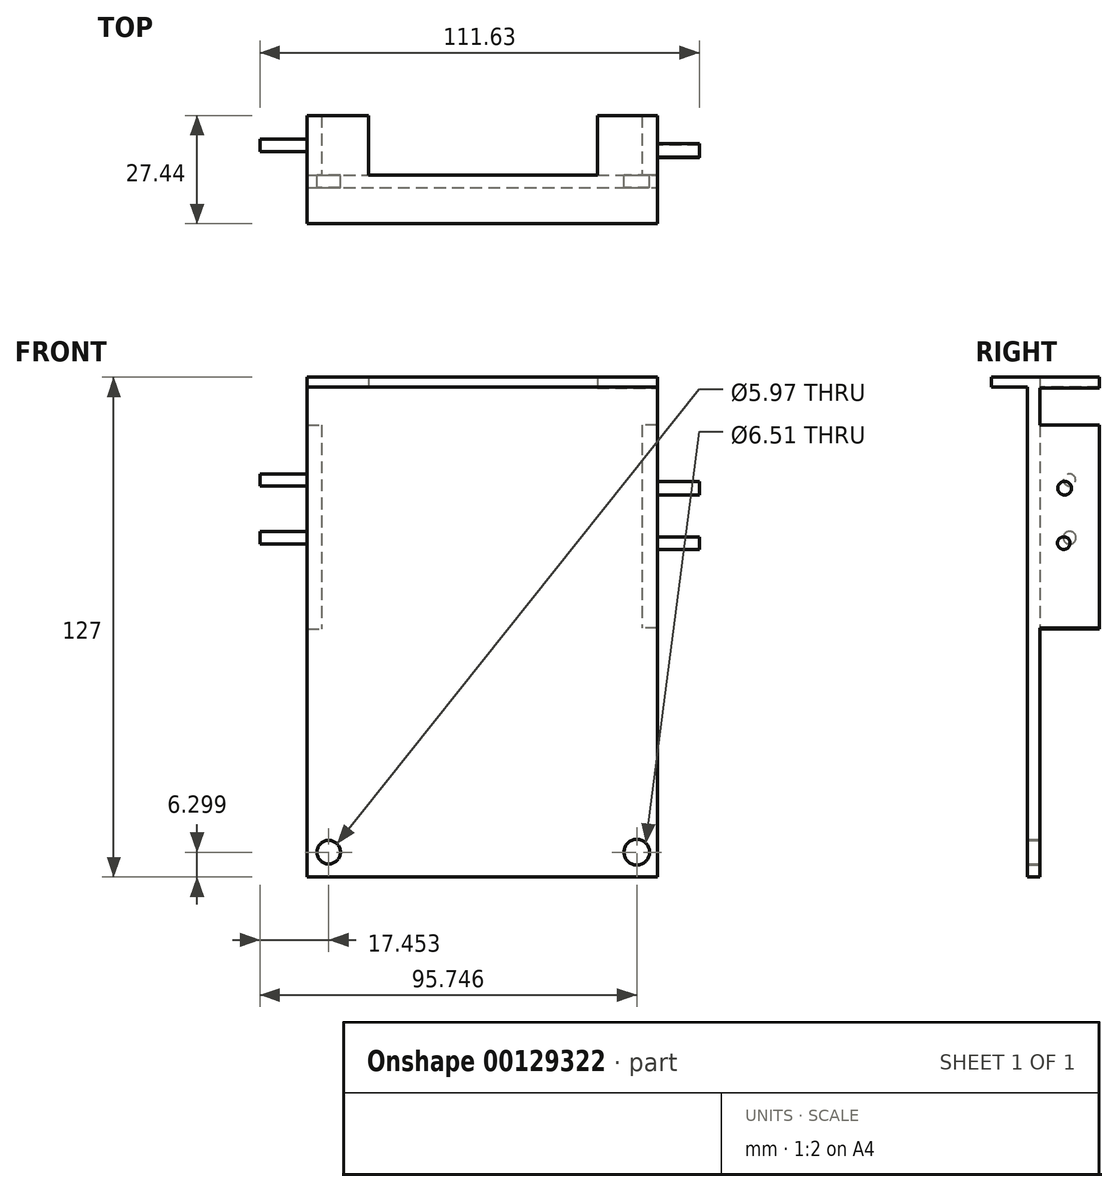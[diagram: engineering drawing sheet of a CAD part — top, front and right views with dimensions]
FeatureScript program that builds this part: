
annotation { "Feature Type Name" : "Feature", "Feature Type Description" : "" }
export const myFeature = defineFeature(function(context is Context, id is Id, definition is map)
    precondition{}
    {
        {
            var Q0;
            Q0=qCreatedBy(makeId("Front.planeOp"),FACE);
            var sketch = newSketch(context, id + "F0", { "sketchPlane" : qUnion([Q0])});
            skLineSegment(sketch, "E0.bottom", {"start": v(-44.56, 55.8) * mm, "end": v(44.34, 55.8) * mm});
            skLineSegment(sketch, "E0.top", {"start": v(-44.56, -71.2) * mm, "end": v(44.34, -71.2) * mm});
            skLineSegment(sketch, "E0.left", {"start": v(-44.56, 55.8) * mm, "end": v(-44.56, -71.2) * mm});
            skLineSegment(sketch, "E0.right", {"start": v(44.34, 55.8) * mm, "end": v(44.34, -71.2) * mm});
            skCircle(sketch, "E1", {"center": v(-39.15, -64.9) * mm, "radius": 2.98 * mm});
            skCircle(sketch, "E2", {"center": v(39.15, -64.9) * mm, "radius": 3.25 * mm});
            skSolve(sketch);
        }
        {
            var Q0;
            Q0=makeQuery(id+"F0.imprint","IMPRINT",FACE,{"disambiguationData":[TD([[makeQuery(id+"F0.imprint","IMPRINT",EDGE,{"derivedFrom":sQuery(id+"F0.wireOp",EDGE,"E0.bottom")}),-1.0]])]});
            extrude(context, id + "F1", {"entities" : qUnion([Q0]), "depth" : 3.17 * mm});
        }
        {
            var Q0;
            Q0=makeQuery(id+"F1.opExtrude","CAP_FACE",FACE,{"disambiguationData":[OSD([sQuery(id+"F0.wireOp",EDGE,"E0.bottom"),sQuery(id+"F0.wireOp",EDGE,"E0.top"),sQuery(id+"F0.wireOp",EDGE,"E0.left"),sQuery(id+"F0.wireOp",EDGE,"E0.right")])],"isStart":false});
            var sketch = newSketch(context, id + "F2", { "sketchPlane" : qUnion([Q0])});
            skLineSegment(sketch, "E3.bottom", {"start": v(-44.56, 55.8) * mm, "end": v(44.34, 55.8) * mm});
            skLineSegment(sketch, "E3.top", {"start": v(-44.56, 53.26) * mm, "end": v(44.34, 53.26) * mm});
            skLineSegment(sketch, "E3.left", {"start": v(-44.56, 55.8) * mm, "end": v(-44.56, 53.26) * mm});
            skLineSegment(sketch, "E3.right", {"start": v(44.34, 55.8) * mm, "end": v(44.34, 53.26) * mm});
            skSolve(sketch);
        }
        {
            var Q0;
            Q0=makeQuery(id+"F2.imprint","IMPRINT",FACE,{"disambiguationData":[TD([[makeQuery(id+"F2.imprint","IMPRINT",EDGE,{"derivedFrom":sQuery(id+"F2.wireOp",EDGE,"E3.bottom")}),-1.0]])]});
            extrude(context, id + "F3", {"entities" : qUnion([Q0]), "operationType" : NewBodyOperationType.ADD, "depth" : 9.15 * mm});
        }
        {
            var Q0;
            Q0=makeQuery(id+"F1.opExtrude","CAP_FACE",FACE,{"disambiguationData":[OSD([sQuery(id+"F0.wireOp",EDGE,"E0.bottom"),sQuery(id+"F0.wireOp",EDGE,"E0.top"),sQuery(id+"F0.wireOp",EDGE,"E0.left"),sQuery(id+"F0.wireOp",EDGE,"E0.right")])],"isStart":true});
            var sketch = newSketch(context, id + "F4", { "sketchPlane" : qUnion([Q0])});
            skLineSegment(sketch, "E4.left", {"start": v(-29.1, 55.8) * mm, "end": v(-29.1, 55.42) * mm});
            skLineSegment(sketch, "E4.right", {"start": v(-44.34, 55.8) * mm, "end": v(-44.34, 55.42) * mm});
            skLineSegment(sketch, "E5.bottom", {"start": v(-41.66, 55.42) * mm, "end": v(-44.34, 55.42) * mm});
            skLineSegment(sketch, "E6.bottom", {"start": v(-29.1, 55.8) * mm, "end": v(-44.34, 55.8) * mm});
            skLineSegment(sketch, "E6.top", {"start": v(-29.1, 53) * mm, "end": v(-44.34, 53) * mm});
            skLineSegment(sketch, "E6.left", {"start": v(-29.1, 55.8) * mm, "end": v(-29.1, 53) * mm});
            skLineSegment(sketch, "E6.right", {"start": v(-44.34, 55.8) * mm, "end": v(-44.34, 53) * mm});
            skLineSegment(sketch, "E7.bottom", {"start": v(44.56, 55.8) * mm, "end": v(29.07, 55.8) * mm});
            skLineSegment(sketch, "E7.top", {"start": v(44.56, 53.23) * mm, "end": v(29.07, 53.23) * mm});
            skLineSegment(sketch, "E7.left", {"start": v(44.56, 55.8) * mm, "end": v(44.56, 53.23) * mm});
            skLineSegment(sketch, "E7.right", {"start": v(29.07, 55.8) * mm, "end": v(29.07, 53.23) * mm});
            skLineSegment(sketch, "E8.bottom", {"start": v(40.75, 53.23) * mm, "end": v(44.56, 53.23) * mm});
            skLineSegment(sketch, "E9.bottom", {"start": v(-29.1, 53) * mm, "end": v(-32.28, 53) * mm});
            skLineSegment(sketch, "E9.top", {"start": v(-29.1, 38.57) * mm, "end": v(-32.28, 38.57) * mm});
            skLineSegment(sketch, "E9.left", {"start": v(-29.1, 53) * mm, "end": v(-29.1, 38.57) * mm});
            skLineSegment(sketch, "E9.right", {"start": v(-32.28, 53) * mm, "end": v(-32.28, 38.57) * mm});
            skLineSegment(sketch, "E10.bottom", {"start": v(29.07, 53.23) * mm, "end": v(32.05, 53.23) * mm});
            skLineSegment(sketch, "E10.top", {"start": v(29.07, 39.03) * mm, "end": v(32.05, 39.03) * mm});
            skLineSegment(sketch, "E10.left", {"start": v(29.07, 53.23) * mm, "end": v(29.07, 39.03) * mm});
            skLineSegment(sketch, "E10.right", {"start": v(32.05, 53.23) * mm, "end": v(32.05, 39.03) * mm});
            skLineSegment(sketch, "E11.bottom", {"start": v(-44.34, 43.61) * mm, "end": v(-40.52, 43.61) * mm});
            skLineSegment(sketch, "E11.top", {"start": v(-44.34, -7.9) * mm, "end": v(-40.52, -7.9) * mm});
            skLineSegment(sketch, "E11.left", {"start": v(-44.34, 43.61) * mm, "end": v(-44.34, -7.9) * mm});
            skLineSegment(sketch, "E11.right", {"start": v(-40.52, 43.61) * mm, "end": v(-40.52, -7.9) * mm});
            skLineSegment(sketch, "E12.bottom", {"start": v(44.56, 43.61) * mm, "end": v(40.98, 43.61) * mm});
            skLineSegment(sketch, "E12.top", {"start": v(44.56, -8.13) * mm, "end": v(40.98, -8.13) * mm});
            skLineSegment(sketch, "E12.left", {"start": v(44.56, 43.61) * mm, "end": v(44.56, -8.13) * mm});
            skLineSegment(sketch, "E12.right", {"start": v(40.98, 43.61) * mm, "end": v(40.98, -8.13) * mm});
            skSolve(sketch);
        }
        {
            var Q0;
            {var subQ5=sQuery(id+"F4.wireOp",EDGE,"E6.bottom");Q0=makeQuery(id+"F4.imprint","IMPRINT",FACE,{"disambiguationData":[TD([[makeQuery(id+"F4.imprint","IMPRINT",EDGE,{"derivedFrom":subQ5}),1.0]])]});}
            var Q1;
            Q1=makeQuery(id+"F4.imprint","IMPRINT",FACE,{"disambiguationData":[TD([[makeQuery(id+"F4.imprint","IMPRINT",EDGE,{"derivedFrom":sQuery(id+"F4.wireOp",EDGE,"E9.bottom")}),1.0]])]});
            var Q2;
            Q2=makeQuery(id+"F4.imprint","IMPRINT",FACE,{"disambiguationData":[TD([[makeQuery(id+"F4.imprint","IMPRINT",EDGE,{"derivedFrom":sQuery(id+"F4.wireOp",EDGE,"E11.bottom")}),-1.0]])]});
            var Q3;
            Q3=makeQuery(id+"F4.imprint","IMPRINT",FACE,{"disambiguationData":[TD([[makeQuery(id+"F4.imprint","IMPRINT",EDGE,{"derivedFrom":sQuery(id+"F4.wireOp",EDGE,"E7.bottom")}),1.0]])]});
            var Q4;
            Q4=makeQuery(id+"F4.imprint","IMPRINT",FACE,{"disambiguationData":[TD([[makeQuery(id+"F4.imprint","IMPRINT",EDGE,{"derivedFrom":sQuery(id+"F4.wireOp",EDGE,"E10.bottom")}),-1.0]])]});
            var Q5;
            Q5=makeQuery(id+"F4.imprint","IMPRINT",FACE,{"disambiguationData":[TD([[makeQuery(id+"F4.imprint","IMPRINT",EDGE,{"derivedFrom":sQuery(id+"F4.wireOp",EDGE,"E12.bottom")}),1.0]])]});
            extrude(context, id + "F5", {"entities" : qUnion([Q0, Q1, Q2, Q3, Q4, Q5]), "operationType" : NewBodyOperationType.ADD, "depth" : 15.12 * mm});
        }
        {
            var Q0;
            Q0=makeQuery(id+"F5.boolean.opBoolean","MERGE",FACE,{"derivedFrom":[makeQuery(id+"F3.boolean.opBoolean","MERGE",FACE,{"derivedFrom":[makeQuery(id+"F1.opExtrude","SWEPT_FACE",FACE,{"disambiguationData":[OSD([sQuery(id+"F0.wireOp",EDGE,"E0.right")])]}),makeQuery(id+"F3.opExtrude","SWEPT_FACE",FACE,{"disambiguationData":[OSD([sQuery(id+"F2.wireOp",EDGE,"E3.right")])]})]}),makeQuery(id+"F5.opExtrude","SWEPT_FACE",FACE,{"disambiguationData":[OSD([sQuery(id+"F4.wireOp",EDGE,"E6.right")])]}),makeQuery(id+"F5.opExtrude","SWEPT_FACE",FACE,{"disambiguationData":[OSD([sQuery(id+"F4.wireOp",EDGE,"E11.left")])]})]});
            var sketch = newSketch(context, id + "F6", { "sketchPlane" : qUnion([Q0])});
            skCircle(sketch, "E13", {"center": v(6.3, 27.59) * mm, "radius": 1.74 * mm});
            skCircle(sketch, "E14", {"center": v(6.07, 13.62) * mm, "radius": 1.6 * mm});
            skSolve(sketch);
        }
        {
            var Q0;
            Q0=makeQuery(id+"F6.imprint","IMPRINT",FACE,{"disambiguationData":[TD([[makeQuery(id+"F6.imprint","IMPRINT",EDGE,{"derivedFrom":sQuery(id+"F6.wireOp",EDGE,"E13")}),1.0]])]});
            var Q1;
            Q1=makeQuery(id+"F6.imprint","IMPRINT",FACE,{"disambiguationData":[TD([[makeQuery(id+"F6.imprint","IMPRINT",EDGE,{"derivedFrom":sQuery(id+"F6.wireOp",EDGE,"E14")}),1.0]])]});
            extrude(context, id + "F7", {"entities" : qUnion([Q0, Q1]), "operationType" : NewBodyOperationType.ADD, "depth" : 10.7 * mm});
        }
        {
            var Q0;
            Q0=makeQuery(id+"F5.boolean.opBoolean","MERGE",FACE,{"derivedFrom":[makeQuery(id+"F3.boolean.opBoolean","MERGE",FACE,{"derivedFrom":[makeQuery(id+"F1.opExtrude","SWEPT_FACE",FACE,{"disambiguationData":[OSD([sQuery(id+"F0.wireOp",EDGE,"E0.left")])]}),makeQuery(id+"F3.opExtrude","SWEPT_FACE",FACE,{"disambiguationData":[OSD([sQuery(id+"F2.wireOp",EDGE,"E3.left")])]})]}),makeQuery(id+"F5.opExtrude","SWEPT_FACE",FACE,{"disambiguationData":[OSD([sQuery(id+"F4.wireOp",EDGE,"E7.left")])]}),makeQuery(id+"F5.opExtrude","SWEPT_FACE",FACE,{"disambiguationData":[OSD([sQuery(id+"F4.wireOp",EDGE,"E12.left")])]})]});
            var sketch = newSketch(context, id + "F8", { "sketchPlane" : qUnion([Q0])});
            skCircle(sketch, "E15", {"center": v(-7.55, 29.65) * mm, "radius": 1.54 * mm});
            skCircle(sketch, "E16", {"center": v(-7.55, 15) * mm, "radius": 1.62 * mm});
            skSolve(sketch);
        }
        {
            var Q0;
            Q0=makeQuery(id+"F8.imprint","IMPRINT",FACE,{"disambiguationData":[TD([[makeQuery(id+"F8.imprint","IMPRINT",EDGE,{"derivedFrom":sQuery(id+"F8.wireOp",EDGE,"E15")}),1.0]])]});
            var Q1;
            Q1=makeQuery(id+"F8.imprint","IMPRINT",FACE,{"disambiguationData":[TD([[makeQuery(id+"F8.imprint","IMPRINT",EDGE,{"derivedFrom":sQuery(id+"F8.wireOp",EDGE,"E16")}),1.0]])]});
            extrude(context, id + "F9", {"entities" : qUnion([Q0, Q1]), "operationType" : NewBodyOperationType.ADD, "depth" : 12.04 * mm});
        }
    });
